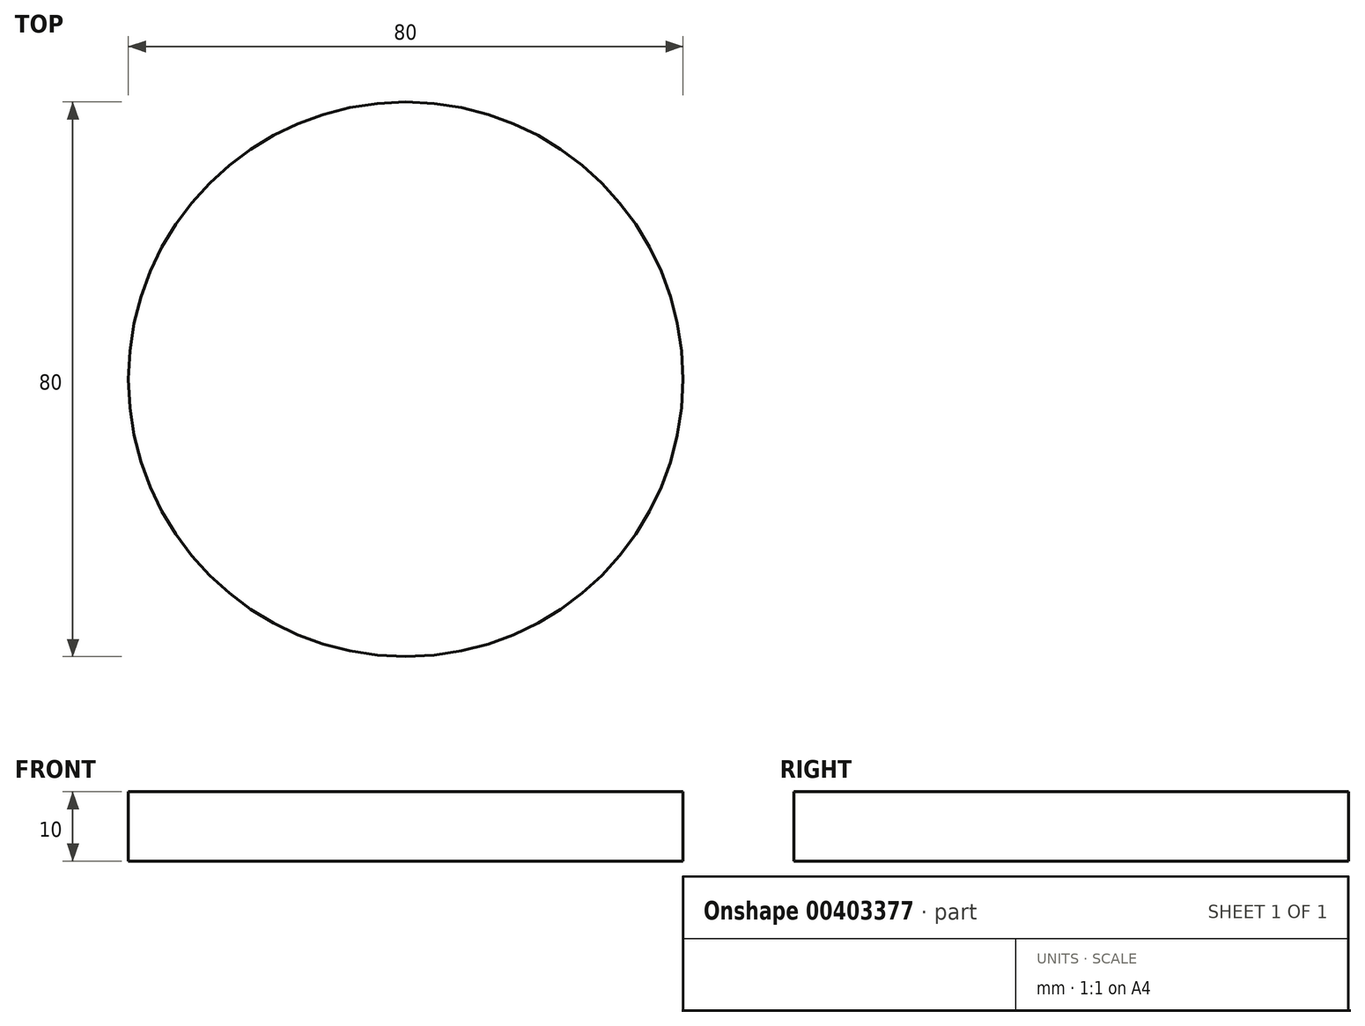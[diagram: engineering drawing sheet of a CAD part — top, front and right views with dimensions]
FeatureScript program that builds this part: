
annotation { "Feature Type Name" : "Feature", "Feature Type Description" : "" }
export const myFeature = defineFeature(function(context is Context, id is Id, definition is map)
    precondition{}
    {
        {
            var Q0;
            Q0=qCreatedBy(makeId("Top.planeOp"),FACE);
            var sketch = newSketch(context, id + "F0", { "sketchPlane" : qUnion([Q0])});
            skCircle(sketch, "E0", {"center": v(0, 0) * mm, "radius": 40 * mm});
            skSolve(sketch);
        }
        {
            var Q0;
            Q0=makeQuery(id+"F0.imprint","IMPRINT",FACE,{"disambiguationData":[TD([[makeQuery(id+"F0.imprint","IMPRINT",EDGE,{"derivedFrom":sQuery(id+"F0.wireOp",EDGE,"E0")}),1.0]])]});
            extrude(context, id + "F1", {"entities" : qUnion([Q0]), "endBound" : BoundingType.SYMMETRIC, "depth" : 10 * mm});
        }
    });
